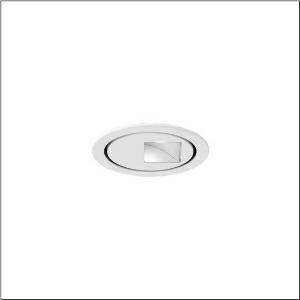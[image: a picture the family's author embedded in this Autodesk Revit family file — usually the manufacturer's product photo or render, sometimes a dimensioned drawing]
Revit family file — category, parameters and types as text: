
# Revit family: lunis_11_micro_round_51dj11cd1wm21
name_source: partatom
category: Lighting Fixtures
units: mm (PartAtom-declared; Revit-internal decimal feet)

## family parameters
Cut with Voids When Loaded = No
Host = Face
Light Source = No
Part Type = Normal
Room Calculation Point = No
Round Connector Dimension = Use Diameter
Shared = No

## types (1)
- Lunis 11 micro round (1 x LED 3000K / CRI = 90 (unbekannt), 1100 lm, 3000K)
    Apparent Load = 20 VA
    CIE Flux Codes = 42 75 96 100 100
    Color Rendering = 90
    Color Temperature = 3000K
    Default Elevation = 1800 mm
    Description = Lunis 11 micro round, downlight, light control with wallwasher, of highly reflective aluminium, highly specular, light emission: direct distribution, LED rated luminous flux: 1.100lm, light colour: 930, control gear: ECG, with terminal, 5-pole, mains connection: 220..230V, AC/DC, 0/50..60Hz, LED module, luminaire module, of aluminium, highly specular, white, diameter: 114mm, clamping range: 1..40mm, recessing ring, of plastic, traffic white (RAL 9016), protection rating (complete): IP20, insulation class (complete): insulation class II (safety insulation), certification: CE, permissible ambient temperature for indoor applications: 0..+35°C, packaging unit: 1 piece
    Height = 0 mm  [stored 0 ft]
    Lamp = 1 x LED 3000K / CRI >= 90 (unbekannt)
    Lamp Light Flux = 1100 lm
    Lamp count = 1
    Length = 114 mm
    Luminous efficacy = 56 lm/W
    Manufacturer = Siteco
    ModVariant = No
    Model = 51DJ11CD1WM21
    Mounting Place = Ceiling
    Mounting Type = Recessed
    Number of Poles = 1
    OnlyDefault = Yes
    Power Factor = 1
    Product Name = Lunis 11 micro round
    Product group = downlight | ceiling recessed
    ProductGroupID = 402
    Protection Class = Protection class II
    Protection Degree = IP 20
    RLX_Detail_Level = 1
    RlxData = <blob elided: 40517 chars, md5=102f3254>
    Socket = socket
    Standby Power = 0 W
    System Light Flux = 1100 lm
    System Power = 20 W
    Type Comments = Product without accessories
    Type Image = l_1004773.jpg
    URL = http://relux.com
    VarID = ---
    Voltage = 0 V
    Weight = 0.00 kg
    Width = 114 mm

note: [stored X ft] marks values corroborated as IEEE doubles in the binary element streams (Revit-internal decimal feet)

## geometry (parser evidence)
native form markers: Blend x4, Sweep x10
no freeform markers — native parametric forms only
